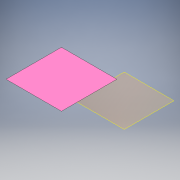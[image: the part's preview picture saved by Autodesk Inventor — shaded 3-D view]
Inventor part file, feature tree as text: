
AUTODESK INVENTOR PART (.ipt)
format: ipt  version: 2018.3 (Build 223284000, 284)  size: 123,904 bytes
history: native  units: mm
features: extrude x2, sketch x2, plane x1, chamfer x1
ambient origin geometry x8: Origin, YZ Plane, XZ Plane, XY Plane, X Axis, Y Axis, Z Axis, Center Point
bodies: Body1 (feature_tree)
feature tree (6):
  plane  "Arbeitsebene1"
  extrude  "Extrusion2"  Depth=18.0mm
  chamfer  "Fase2"  Distance=18.0mm
  extrude  "Extrusion3"  Depth=55.0mm
  sketch  "Skizze2"  dims[d5=540.0mm d6=540.0mm d7=18.0mm d8=0.0mm]
  sketch  "Skizze3"  dims[d9=18.0mm d10=2.0mm d11=45.0deg d12=55.0mm d13=110.0mm d14=20.0mm d15=20.0mm d16=4.0mm d17=15.0mm d18=0.0mm]
